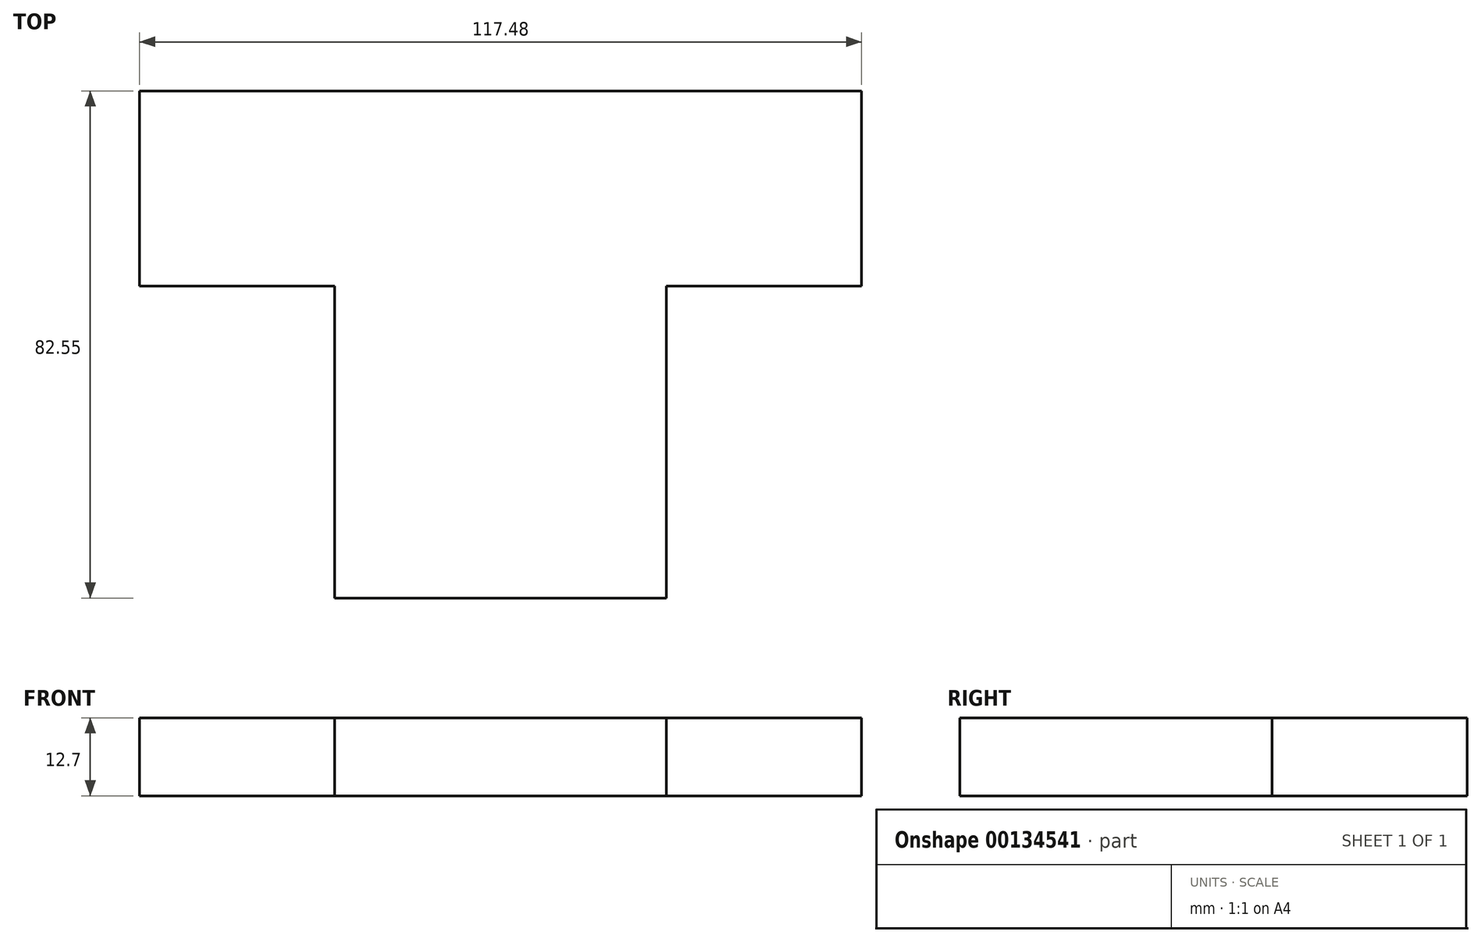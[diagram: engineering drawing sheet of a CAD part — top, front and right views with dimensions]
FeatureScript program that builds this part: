
annotation { "Feature Type Name" : "Feature", "Feature Type Description" : "" }
export const myFeature = defineFeature(function(context is Context, id is Id, definition is map)
    precondition{}
    {
        {
            var Q0;
            Q0=qCreatedBy(makeId("Top.planeOp"),FACE);
            var sketch = newSketch(context, id + "F0", { "sketchPlane" : qUnion([Q0])});
            skLineSegment(sketch, "E0", {"start": v(-30.38, 14.5) * mm, "end": v(87.1, 14.5) * mm});
            skLineSegment(sketch, "E1", {"start": v(87.1, 14.5) * mm, "end": v(87.1, -17.26) * mm});
            skLineSegment(sketch, "E2", {"start": v(87.1, -17.26) * mm, "end": v(55.35, -17.26) * mm});
            skLineSegment(sketch, "E3", {"start": v(55.35, -17.26) * mm, "end": v(55.35, -68.06) * mm});
            skLineSegment(sketch, "E4", {"start": v(55.35, -68.06) * mm, "end": v(1.37, -68.06) * mm});
            skLineSegment(sketch, "E5", {"start": v(1.37, -68.06) * mm, "end": v(1.37, -17.26) * mm});
            skLineSegment(sketch, "E6", {"start": v(1.37, -17.26) * mm, "end": v(-30.38, -17.26) * mm});
            skLineSegment(sketch, "E7", {"start": v(-30.38, -17.26) * mm, "end": v(-30.38, 14.5) * mm});
            skSolve(sketch);
        }
        {
            var Q0;
            Q0=makeQuery(id+"F0.imprint","IMPRINT",FACE,{"disambiguationData":[TD([[makeQuery(id+"F0.imprint","IMPRINT",EDGE,{"derivedFrom":sQuery(id+"F0.wireOp",EDGE,"E0")}),-1.0]])]});
            extrude(context, id + "F1", {"entities" : qUnion([Q0]), "depth" : 12.7 * mm});
        }
    });
